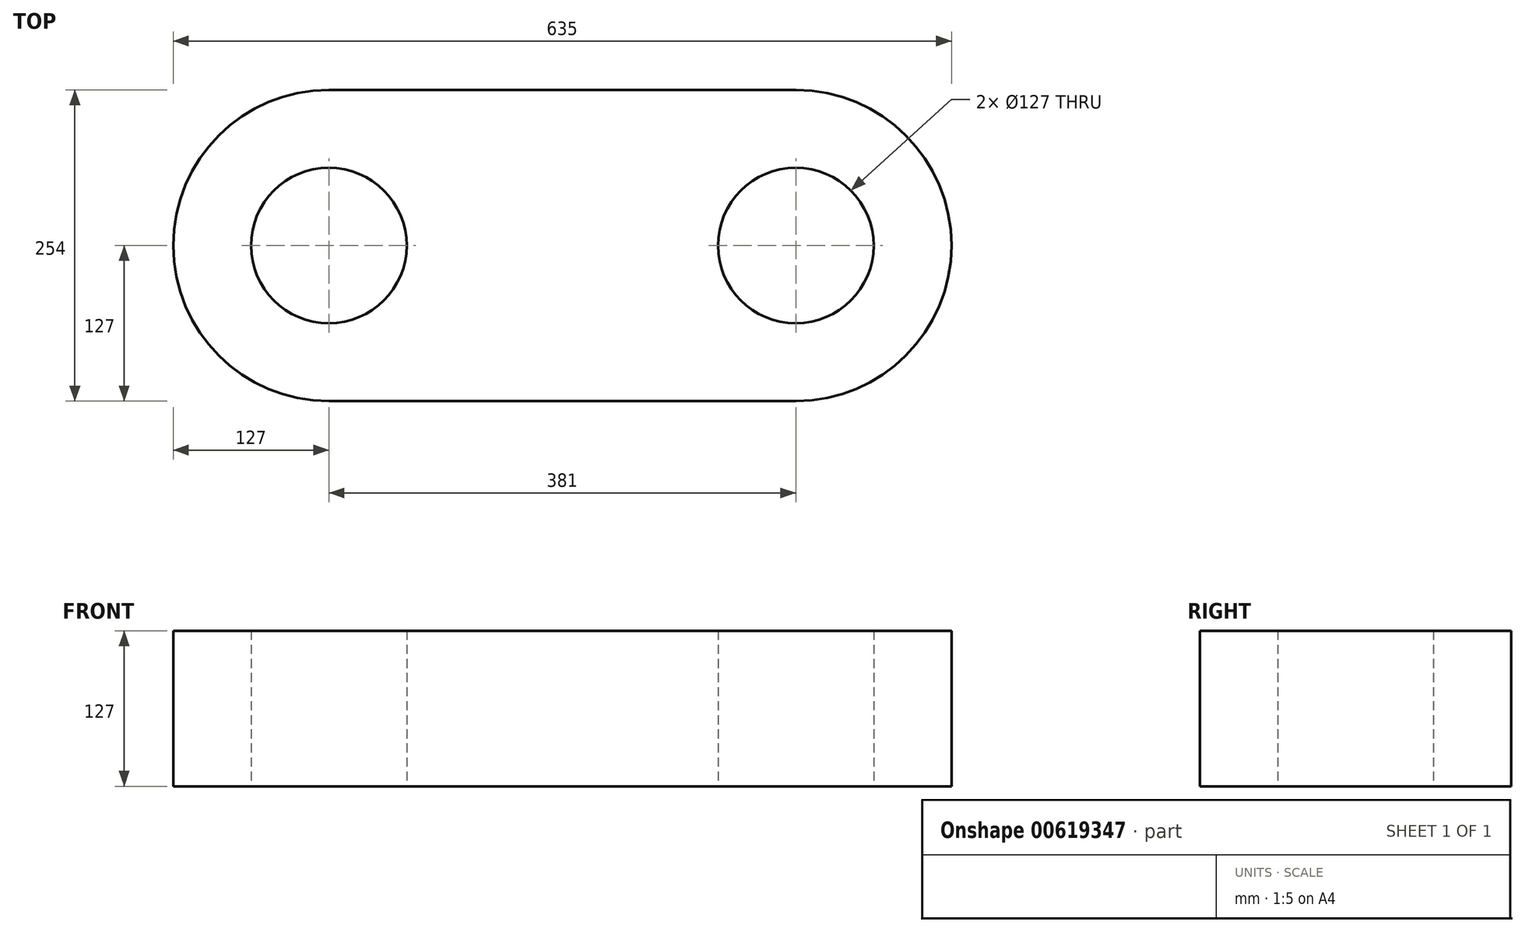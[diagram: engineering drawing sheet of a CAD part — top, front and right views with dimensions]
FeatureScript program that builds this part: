
annotation { "Feature Type Name" : "Feature", "Feature Type Description" : "" }
export const myFeature = defineFeature(function(context is Context, id is Id, definition is map)
    precondition{}
    {
        {
            var Q0;
            Q0=qCreatedBy(makeId("Top.planeOp"),FACE);
            var sketch = newSketch(context, id + "F0", { "sketchPlane" : qUnion([Q0])});
            skLineSegment(sketch, "E0.bottom", {"start": v(-190.5, 127) * mm, "end": v(190.5, 127) * mm});
            skLineSegment(sketch, "E0.top", {"start": v(-190.5, -127) * mm, "end": v(190.5, -127) * mm});
            skArc(sketch, "E1", {"start": v(190.5, -127) * mm, "mid": v(317.5, 0) * mm, "end": v(190.5, 127) * mm});
            skArc(sketch, "E2", {"start": v(-190.5, 127) * mm, "mid": v(-317.5, 0) * mm, "end": v(-190.5, -127) * mm});
            skCircle(sketch, "E3", {"center": v(-190.5, 0) * mm, "radius": 63.5 * mm});
            skCircle(sketch, "E4", {"center": v(190.5, 0) * mm, "radius": 63.5 * mm});
            skSolve(sketch);
        }
        {
            var Q0;
            Q0 = qSketchRegion(id + "F0", true);
            extrude(context, id + "F1", {"entities" : qUnion([Q0]), "depth" : 127 * mm, "offsetDistance" : 25.4 * mm});
        }
    });
